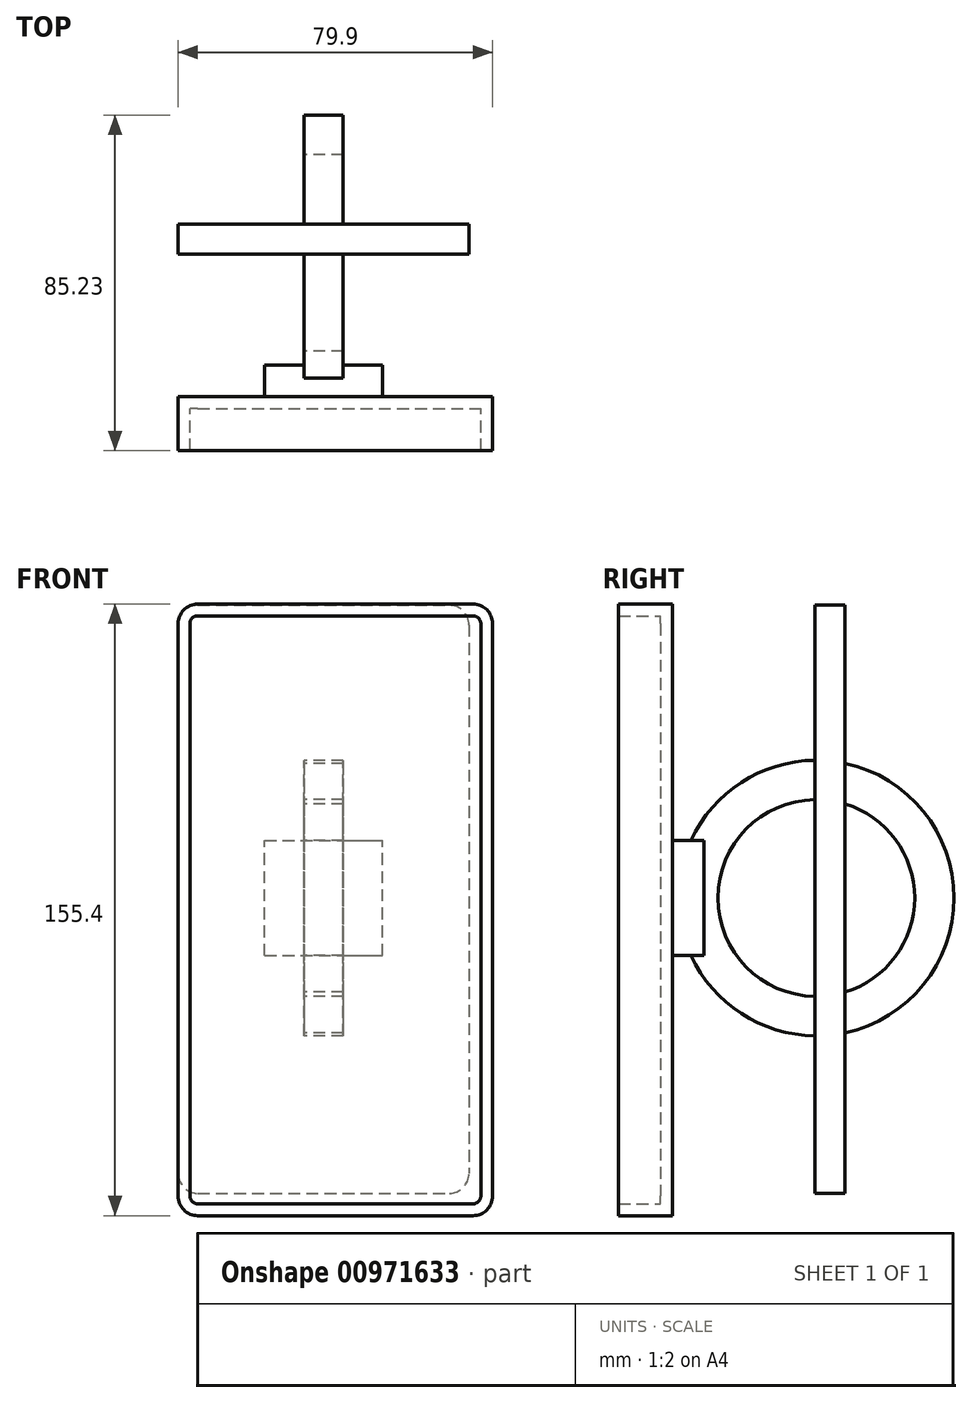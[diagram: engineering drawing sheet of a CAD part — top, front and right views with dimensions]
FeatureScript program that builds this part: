
annotation { "Feature Type Name" : "Feature", "Feature Type Description" : "" }
export const myFeature = defineFeature(function(context is Context, id is Id, definition is map)
    precondition{}
    {
        {
            var Q0;
            Q0=qCreatedBy(makeId("Front.planeOp"),FACE);
            var sketch = newSketch(context, id + "F0", { "sketchPlane" : qUnion([Q0])});
            skLineSegment(sketch, "E0.bottom", {"start": v(-36.95, 149.4) * mm, "end": v(36.95, 149.4) * mm});
            skLineSegment(sketch, "E0.top", {"start": v(-36.95, 0) * mm, "end": v(36.95, 0) * mm});
            skLineSegment(sketch, "E0.left", {"start": v(-36.95, 149.4) * mm, "end": v(-36.95, 0) * mm});
            skLineSegment(sketch, "E0.right", {"start": v(36.95, 149.4) * mm, "end": v(36.95, 0) * mm});
            skSolve(sketch);
        }
        {
            var Q0;
            Q0=makeQuery(id+"F0.imprint","IMPRINT",FACE,{"disambiguationData":[TD([[makeQuery(id+"F0.imprint","IMPRINT",EDGE,{"derivedFrom":sQuery(id+"F0.wireOp",EDGE,"E0.bottom")}),-1.0]])]});
            extrude(context, id + "F1", {"entities" : qUnion([Q0]), "endBound" : BoundingType.SYMMETRIC, "depth" : 7.7 * mm, "offsetDistance" : 25 * mm});
        }
        {
            var Q0;
            Q0=makeQuery(id+"F1.opExtrude","SWEPT_BODY",BODY,{"disambiguationData":[OSD([sQuery(id+"F0.wireOp",EDGE,"E0.bottom"),sQuery(id+"F0.wireOp",EDGE,"E0.top"),sQuery(id+"F0.wireOp",EDGE,"E0.left"),sQuery(id+"F0.wireOp",EDGE,"E0.right")])]});
            transform(context, id + "F2", {"entities" : qUnion([Q0]), "transformType" : TransformType.TRANSLATION_3D, "dx" : 0 * mm, "dy" : 0 * mm, "dz" : -75 * mm, "makeCopy" : false});
        }
        {
            var Q0;
            Q0=makeQuery(id+"F1.opExtrude","SWEPT_EDGE",EDGE,{"disambiguationData":[OSD([sQuery(id+"F0.wireOp",EDGE,"E0.bottom"),sQuery(id+"F0.wireOp",EDGE,"E0.right")])]});
            fillet(context, id + "F3", {"entities" : qUnion([Q0]), "radius" : 5 * mm, "tangentPropagation" : true, "allowEdgeOverflow" : false});
        }
        {
            var Q0;
            Q0=makeQuery(id+"F1.opExtrude","SWEPT_EDGE",EDGE,{"disambiguationData":[OSD([sQuery(id+"F0.wireOp",EDGE,"E0.bottom"),sQuery(id+"F0.wireOp",EDGE,"E0.left")])]});
            var Q1;
            Q1=makeQuery(id+"F1.opExtrude","SWEPT_EDGE",EDGE,{"disambiguationData":[OSD([sQuery(id+"F0.wireOp",EDGE,"E0.top"),sQuery(id+"F0.wireOp",EDGE,"E0.left")])]});
            var Q2;
            Q2=makeQuery(id+"F1.opExtrude","SWEPT_EDGE",EDGE,{"disambiguationData":[OSD([sQuery(id+"F0.wireOp",EDGE,"E0.top"),sQuery(id+"F0.wireOp",EDGE,"E0.right")])]});
            fillet(context, id + "F4", {"entities" : qUnion([Q0, Q1, Q2]), "radius" : 5 * mm, "tangentPropagation" : true, "allowEdgeOverflow" : false});
        }
        {
            var Q0;
            Q0=makeQuery(id+"F1.opExtrude","SWEPT_BODY",BODY,{"disambiguationData":[OSD([sQuery(id+"F0.wireOp",EDGE,"E0.bottom"),sQuery(id+"F0.wireOp",EDGE,"E0.top"),sQuery(id+"F0.wireOp",EDGE,"E0.left"),sQuery(id+"F0.wireOp",EDGE,"E0.right")])]});
            transform(context, id + "F5", {"entities" : qUnion([Q0]), "transformType" : TransformType.TRANSLATION_3D, "dx" : 0 * mm, "dy" : 23 * mm, "dz" : 0 * mm, "makeCopy" : true});
        }
        {
            var Q0;
            Q0=makeQuery(id+"F5.opPattern","COPY",BODY,{"derivedFrom":makeQuery(id+"F1.opExtrude","SWEPT_BODY",BODY,{"disambiguationData":[OSD([sQuery(id+"F0.wireOp",EDGE,"E0.bottom"),sQuery(id+"F0.wireOp",EDGE,"E0.top"),sQuery(id+"F0.wireOp",EDGE,"E0.left"),sQuery(id+"F0.wireOp",EDGE,"E0.right")])]}),"instanceName":"1"});
            deleteBodies(context, id + "F6", {"entities" : qUnion([Q0])});
        }
        {
            var Q0;
            Q0=qCreatedBy(makeId("Front.planeOp"),FACE);
            var sketch = newSketch(context, id + "F7", { "sketchPlane" : qUnion([Q0])});
            skLineSegment(sketch, "E1.bottom", {"start": v(-36.95, 74.7) * mm, "end": v(42.95, 74.7) * mm});
            skLineSegment(sketch, "E1.top", {"start": v(-36.95, -80.7) * mm, "end": v(42.95, -80.7) * mm});
            skLineSegment(sketch, "E1.left", {"start": v(-36.95, 74.7) * mm, "end": v(-36.95, -80.7) * mm});
            skLineSegment(sketch, "E1.right", {"start": v(42.95, 74.7) * mm, "end": v(42.95, -80.7) * mm});
            skSolve(sketch);
        }
        {
            var Q0;
            Q0=makeQuery(id+"F1.opExtrude","SWEPT_BODY",BODY,{"disambiguationData":[OSD([sQuery(id+"F0.wireOp",EDGE,"E0.bottom"),sQuery(id+"F0.wireOp",EDGE,"E0.top"),sQuery(id+"F0.wireOp",EDGE,"E0.left"),sQuery(id+"F0.wireOp",EDGE,"E0.right")])]});
            transform(context, id + "F8", {"entities" : qUnion([Q0]), "transformType" : TransformType.TRANSLATION_3D, "dx" : 0 * mm, "dy" : 40 * mm, "dz" : 0 * mm, "makeCopy" : false});
        }
        {
            var Q0;
            Q0=makeQuery(id+"F7.imprint","IMPRINT",FACE,{"disambiguationData":[TD([[makeQuery(id+"F7.imprint","IMPRINT",EDGE,{"derivedFrom":sQuery(id+"F7.wireOp",EDGE,"E1.bottom")}),-1.0]])]});
            extrude(context, id + "F9", {"entities" : qUnion([Q0]), "depth" : 13.7 * mm, "offsetDistance" : 25 * mm});
        }
        {
            var Q0;
            Q0=makeQuery(id+"F9.opExtrude","SWEPT_EDGE",EDGE,{"disambiguationData":[OSD([sQuery(id+"F7.wireOp",EDGE,"E1.bottom"),sQuery(id+"F7.wireOp",EDGE,"E1.left")])]});
            var Q1;
            Q1=makeQuery(id+"F9.opExtrude","SWEPT_EDGE",EDGE,{"disambiguationData":[OSD([sQuery(id+"F7.wireOp",EDGE,"E1.bottom"),sQuery(id+"F7.wireOp",EDGE,"E1.right")])]});
            var Q2;
            Q2=makeQuery(id+"F9.opExtrude","SWEPT_EDGE",EDGE,{"disambiguationData":[OSD([sQuery(id+"F7.wireOp",EDGE,"E1.top"),sQuery(id+"F7.wireOp",EDGE,"E1.right")])]});
            var Q3;
            Q3=makeQuery(id+"F9.opExtrude","SWEPT_EDGE",EDGE,{"disambiguationData":[OSD([sQuery(id+"F7.wireOp",EDGE,"E1.top"),sQuery(id+"F7.wireOp",EDGE,"E1.left")])]});
            fillet(context, id + "F10", {"entities" : qUnion([Q0, Q1, Q2, Q3]), "radius" : 5 * mm, "tangentPropagation" : true, "allowEdgeOverflow" : false});
        }
        {
            var Q0;
            Q0=makeQuery(id+"F9.opExtrude","CAP_FACE",FACE,{"disambiguationData":[OSD([sQuery(id+"F7.wireOp",EDGE,"E1.bottom"),sQuery(id+"F7.wireOp",EDGE,"E1.top"),sQuery(id+"F7.wireOp",EDGE,"E1.left"),sQuery(id+"F7.wireOp",EDGE,"E1.right")])],"isStart":false});
            shell(context, id + "F11", {"entities" : qUnion([Q0]), "thickness" : 3 * mm});
        }
        {
            var Q0;
            Q0=makeQuery(id+"F9.opExtrude","CAP_FACE",FACE,{"disambiguationData":[OSD([sQuery(id+"F7.wireOp",EDGE,"E1.bottom"),sQuery(id+"F7.wireOp",EDGE,"E1.top"),sQuery(id+"F7.wireOp",EDGE,"E1.left"),sQuery(id+"F7.wireOp",EDGE,"E1.right")])],"isStart":true});
            var sketch = newSketch(context, id + "F12", { "sketchPlane" : qUnion([Q0])});
            skLineSegment(sketch, "E2.bottom", {"start": v(15, -14.6) * mm, "end": v(-15, -14.6) * mm});
            skLineSegment(sketch, "E2.top", {"start": v(15, 14.6) * mm, "end": v(-15, 14.6) * mm});
            skLineSegment(sketch, "E2.left", {"start": v(15, -14.6) * mm, "end": v(15, 14.6) * mm});
            skLineSegment(sketch, "E2.right", {"start": v(-15, -14.6) * mm, "end": v(-15, 14.6) * mm});
            skPoint(sketch, "E2.middle", {"position": v(0, 0) * mm});
            skSolve(sketch);
        }
        {
            var Q0;
            Q0=makeQuery(id+"F12.imprint","IMPRINT",FACE,{"disambiguationData":[TD([[makeQuery(id+"F12.imprint","IMPRINT",EDGE,{"derivedFrom":sQuery(id+"F12.wireOp",EDGE,"E2.bottom")}),-1.0]])]});
            extrude(context, id + "F13", {"entities" : qUnion([Q0]), "operationType" : NewBodyOperationType.ADD, "depth" : 8 * mm, "offsetDistance" : 25 * mm});
        }
        {
            var Q0;
            Q0=qCreatedBy(makeId("Top.planeOp"),FACE);
            var sketch = newSketch(context, id + "F14", { "sketchPlane" : qUnion([Q0])});
            skLineSegment(sketch, "E3.bottom", {"start": v(-5, 11.53) * mm, "end": v(5, 11.53) * mm});
            skLineSegment(sketch, "E3.top", {"start": v(-5, 1.53) * mm, "end": v(5, 1.53) * mm});
            skLineSegment(sketch, "E3.left", {"start": v(-5, 11.53) * mm, "end": v(-5, 1.53) * mm});
            skLineSegment(sketch, "E3.right", {"start": v(5, 11.53) * mm, "end": v(5, 1.53) * mm});
            skPoint(sketch, "E3.middle", {"position": v(0, 6.53) * mm});
            skLineSegment(sketch, "E4", {"start": v(-8.64, 36.53) * mm, "end": v(7.86, 36.53) * mm});
            skSolve(sketch);
        }
        {
            var Q0;
            Q0 = qSketchRegion(id + "F14", true);
            var Q1;
            Q1=sQuery(id+"F14.wireOp",EDGE,"E4");
            revolve(context, id + "F15", {"operationType" : NewBodyOperationType.ADD, "surfaceOperationType" : NewSurfaceOperationType.NEW, "entities" : qUnion([Q0]), "axis" : qUnion([Q1]), "revolveType" : RevolveType.FULL});
        }
    });
